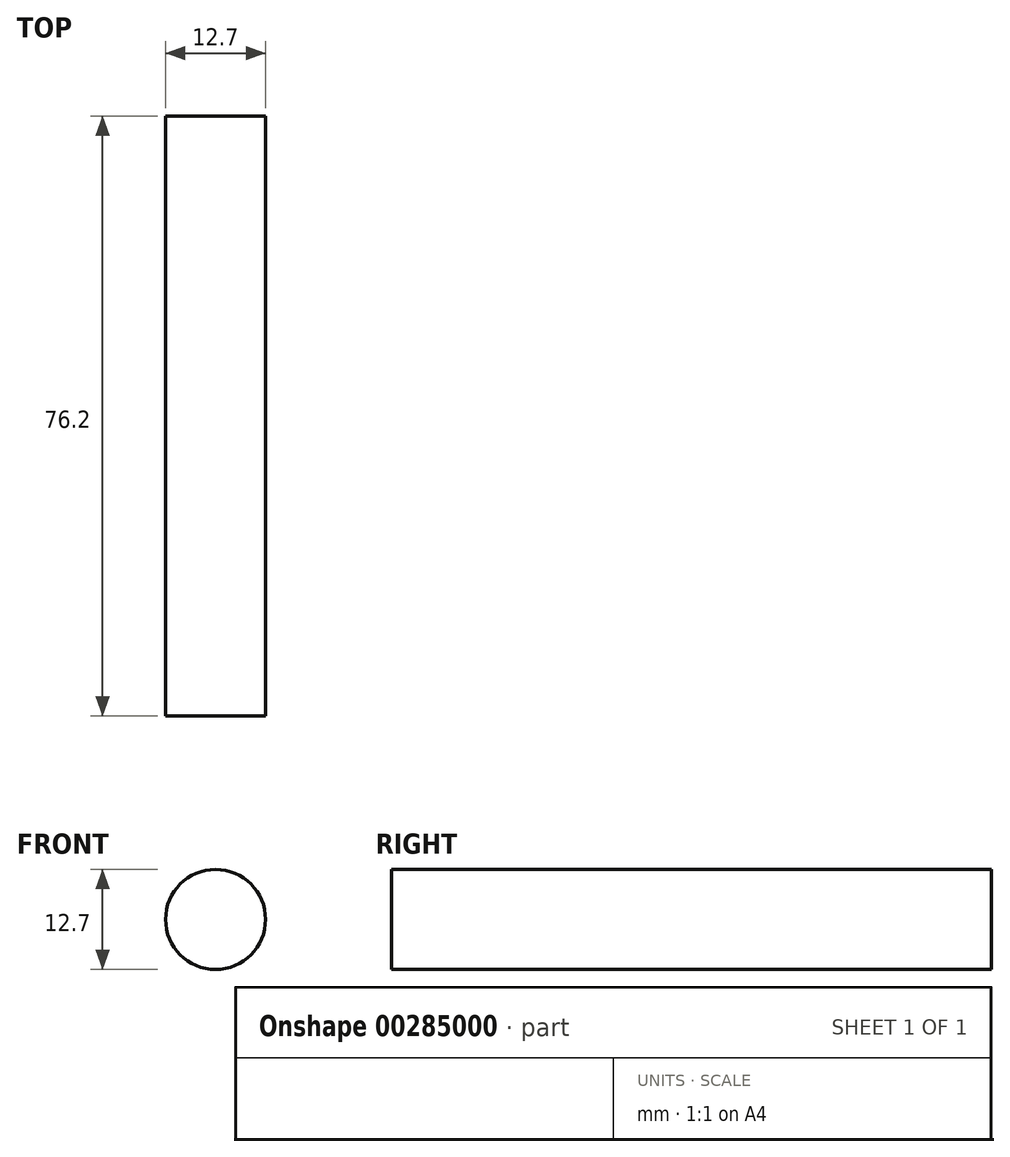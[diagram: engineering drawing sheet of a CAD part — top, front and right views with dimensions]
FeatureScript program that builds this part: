
annotation { "Feature Type Name" : "Feature", "Feature Type Description" : "" }
export const myFeature = defineFeature(function(context is Context, id is Id, definition is map)
    precondition{}
    {
        {
            var Q0;
            Q0=qCreatedBy(makeId("Front.planeOp"),FACE);
            var sketch = newSketch(context, id + "F0", { "sketchPlane" : qUnion([Q0])});
            skCircle(sketch, "E0", {"center": v(-59.5, 40.24) * mm, "radius": 6.35 * mm});
            skSolve(sketch);
        }
        {
            var Q0;
            Q0=makeQuery(id+"F0.imprint","IMPRINT",FACE,{"disambiguationData":[TD([[makeQuery(id+"F0.imprint","IMPRINT",EDGE,{"derivedFrom":sQuery(id+"F0.wireOp",EDGE,"E0")}),1.0]])]});
            extrude(context, id + "F1", {"entities" : qUnion([Q0]), "depth" : 76.2 * mm});
        }
    });
